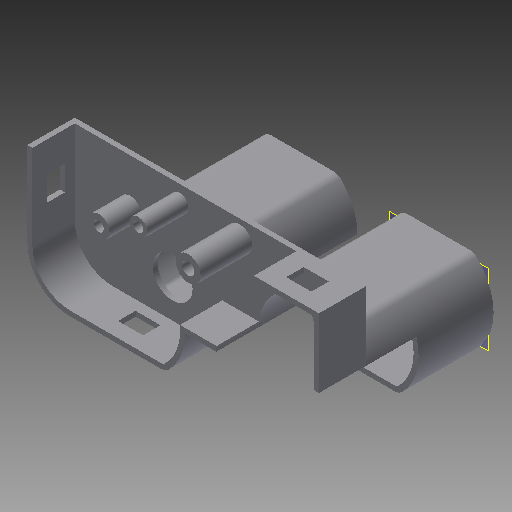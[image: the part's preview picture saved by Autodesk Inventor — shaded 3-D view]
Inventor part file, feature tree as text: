
AUTODESK INVENTOR PART (.ipt)
format: ipt  version: 2017 (Build 210142000, 142)  size: 305,152 bytes
history: native  units: mm
features: extrude x15, sketch x15, plane x15, reference x9
ambient origin geometry x8: Origin, YZ Plane, XZ Plane, XY Plane, X Axis, Y Axis, Z Axis, Center Point
bodies: Solid1 (feature_tree)
feature tree (54):
  extrude  "Extrusion1"  Depth=15.0mm TaperAngle=0.0deg
  sketch  "Sketch2"  dims[d3=15.0mm d4=0.0mm d8=1.0mm]
  plane  "Work Plane1"
  extrude  "Extrusion2"  Depth=1.0mm
  sketch  "Sketch3"  dims[d9=15.0mm d10=0.0mm d11=15.0mm d12=0.0mm]
  plane  "Work Plane2"
  extrude  "Extrusion4"  Depth=15.0mm TaperAngle=0.0deg
  sketch  "Sketch5"  dims[d19=1.0mm d20=0.0mm d29=8.5mm d30=0.0mm]
  plane  "Work Plane3"
  extrude  "Extrusion5"  Depth=1.0mm TaperAngle=0.0deg
  extrude  "Extrusion6"  Depth=8.5mm TaperAngle=0.0deg
  sketch  "Sketch6"  dims[d33=1.0mm d34=10.0mm d35=0.0mm]
  plane  "Work Plane4"
  extrude  "Extrusion7"  Depth=10.0mm TaperAngle=0.0deg
  sketch  "Sketch7"  dims[d36=10.0mm d37=0.0mm d43=10.0mm d44=0.0mm]
  plane  "Work Plane5"
  extrude  "Extrusion8"  Depth=10.0mm TaperAngle=0.0deg
  plane  "Work Plane6"
  plane  "Work Plane7"
  plane  "Work Plane8"
  plane  "Work Plane9"
  extrude  "Extrusion13"  Depth=3.5mm
  sketch  "Sketch13"  dims[d52=1.0mm d53=0.0mm d54=3.5mm]
  plane  "Work Plane10"
  extrude  "Extrusion14"  Depth=3.5mm
  sketch  "Sketch14"  dims[d55=5.0mm d56=1.0mm d57=0.0mm]
  plane  "Work Plane11"
  extrude  "Extrusion15"  Depth=1.0mm TaperAngle=0.0deg
  sketch  "Sketch15"  dims[d58=3.5mm d59=1.0mm d60=0.0mm]
  plane  "Work Plane12"
  plane  "Work Plane13"
  plane  "Work Plane14"
  extrude  "Extrusion18"  Depth=1.0mm TaperAngle=0.0deg
  sketch  "Sketch17"
  plane  "Work Plane15"
  extrude  "Extrusion19"  [1 undecoded]
  extrude  "Extrusion21"  [1 undecoded]
  extrude  "Extrusion22"  [1 undecoded]
  extrude  "Extrusion23"  [1 undecoded]
  sketch  "Sketch1"  dims[d0=1.0mm d1=15.0mm d2=0.0mm]
  sketch  "Sketch4"  dims[d14=1.0mm d15=0.0mm d17=1.0mm d18=0.0mm]
  reference  "Reference18"
  reference  "Reference19"
  sketch  "Sketch12"  dims[d45=10.0mm d46=0.0mm d51=3.5mm]
  reference  "Reference30"
  reference  "Reference31"
  reference  "Reference32"
  reference  "Reference36"
  sketch  "Sketch19"
  reference  "Reference38"
  sketch  "Sketch20"
  reference  "Reference39"
  sketch  "Sketch21"
  reference  "Reference40"
note: 4 required parameter values undecoded (feature->parameter linkage not recoverable at this tier; creation-order binding heuristic only, values carry confidence <= 0.55)
